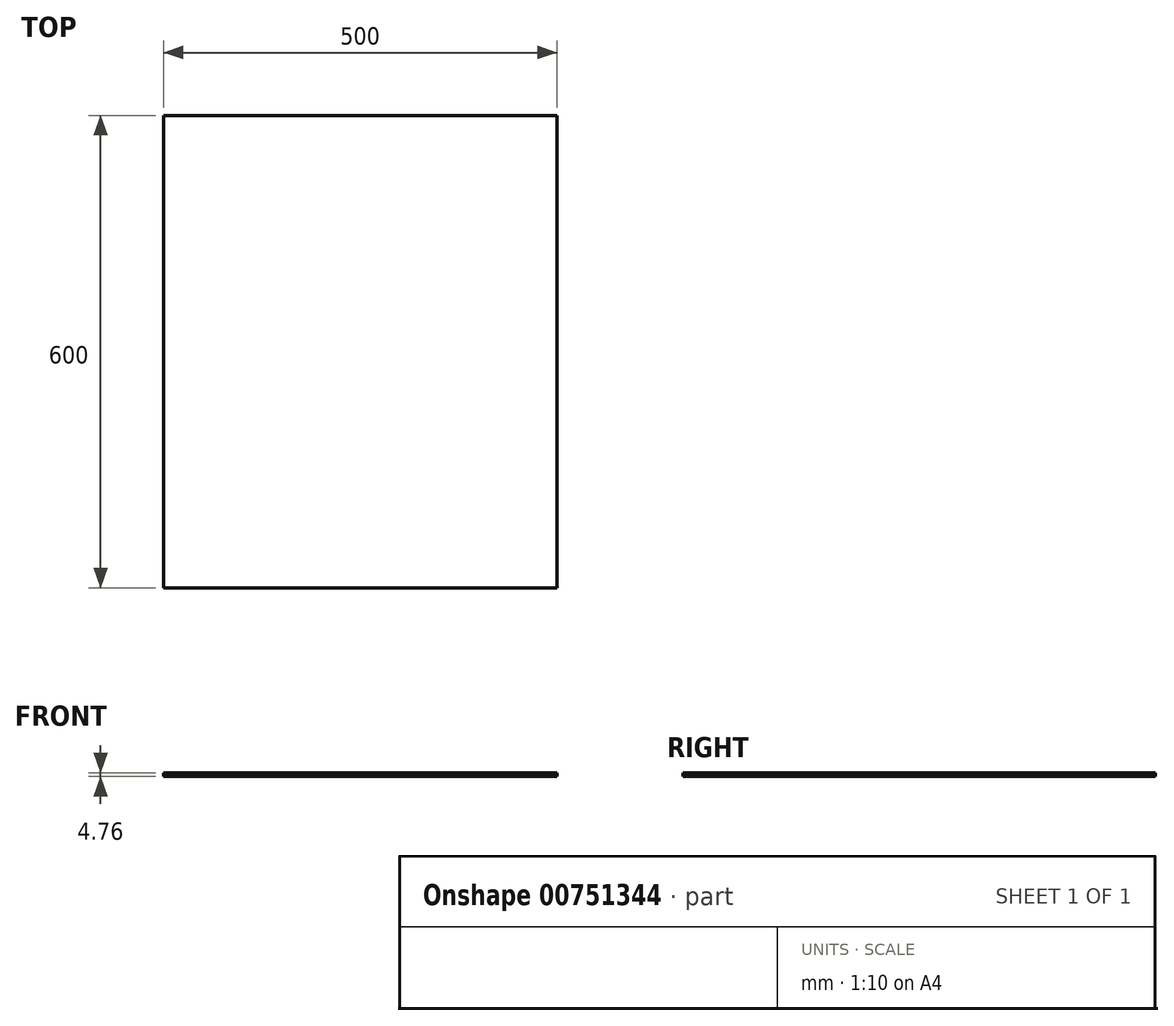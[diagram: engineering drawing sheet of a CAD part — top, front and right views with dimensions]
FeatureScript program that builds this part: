
annotation { "Feature Type Name" : "Feature", "Feature Type Description" : "" }
export const myFeature = defineFeature(function(context is Context, id is Id, definition is map)
    precondition{}
    {
        {
            var Q0;
            Q0=qCreatedBy(makeId("Top.planeOp"),FACE);
            var sketch = newSketch(context, id + "F0", { "sketchPlane" : qUnion([Q0])});
            skLineSegment(sketch, "E0.bottom", {"start": v(-250, -300) * mm, "end": v(250, -300) * mm});
            skLineSegment(sketch, "E0.top", {"start": v(-250, 300) * mm, "end": v(250, 300) * mm});
            skLineSegment(sketch, "E0.left", {"start": v(-250, -300) * mm, "end": v(-250, 300) * mm});
            skLineSegment(sketch, "E0.right", {"start": v(250, -300) * mm, "end": v(250, 300) * mm});
            skPoint(sketch, "E0.middle", {"position": v(0, 0) * mm});
            skSolve(sketch);
        }
        {
            var Q0;
            Q0=makeQuery(id+"F0.imprint","IMPRINT",FACE,{"disambiguationData":[TD([[makeQuery(id+"F0.imprint","IMPRINT",EDGE,{"derivedFrom":sQuery(id+"F0.wireOp",EDGE,"E0.bottom")}),1.0]])]});
            extrude(context, id + "F1", {"entities" : qUnion([Q0]), "depth" : 4.76 * mm, "offsetDistance" : 25 * mm});
        }
    });
